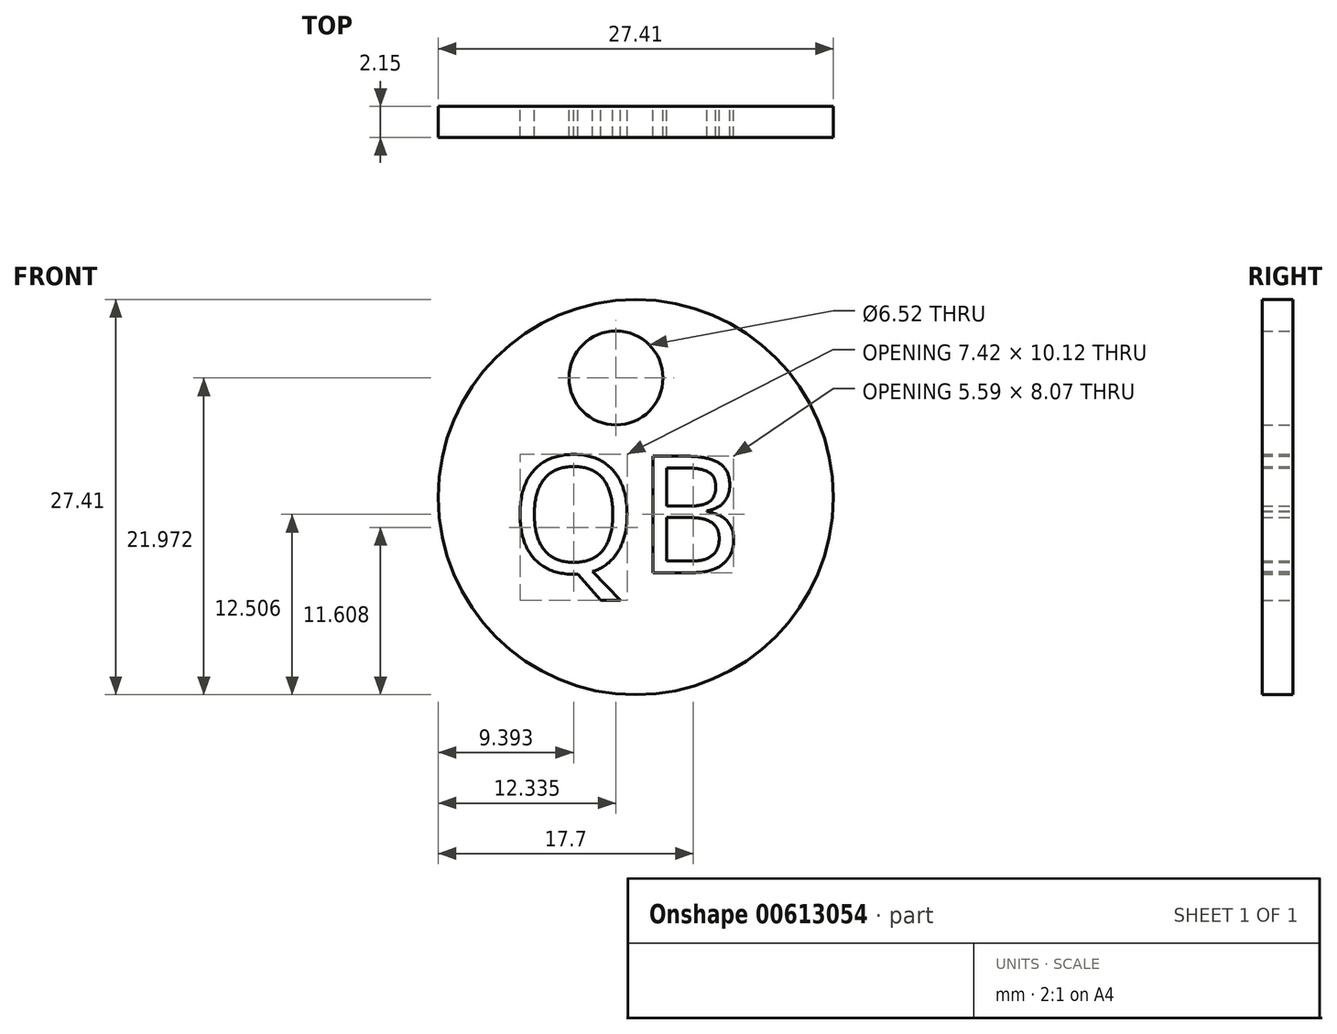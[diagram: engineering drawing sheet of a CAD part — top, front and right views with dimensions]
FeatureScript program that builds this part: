
annotation { "Feature Type Name" : "Feature", "Feature Type Description" : "" }
export const myFeature = defineFeature(function(context is Context, id is Id, definition is map)
    precondition{}
    {
        {
            var Q0;
            Q0=qCreatedBy(makeId("Front.planeOp"),FACE);
            var sketch = newSketch(context, id + "F0", { "sketchPlane" : qUnion([Q0])});
            skCircle(sketch, "E0", {"center": v(-43.44, -15.26) * mm, "radius": 13.7 * mm});
            skPoint(sketch, "E1", {"position": v(-42.95, -1.56) * mm});
            skPoint(sketch, "E2", {"position": v(-43.28, -28.96) * mm});
            skSolve(sketch);
        }
        {
            var Q0;
            Q0 = qSketchRegion(id + "F0", true);
            extrude(context, id + "F1", {"entities" : qUnion([Q0]), "depth" : 2.15 * mm, "offsetDistance" : 25 * mm});
        }
        {
            var Q0;
            Q0=qCreatedBy(makeId("Front.planeOp"),FACE);
            var sketch = newSketch(context, id + "F2", { "sketchPlane" : qUnion([Q0])});
            skCircle(sketch, "E3", {"center": v(-44.82, -6.99) * mm, "radius": 3.26 * mm});
            skSolve(sketch);
        }
        {
            var Q0;
            Q0 = qSketchRegion(id + "F2", true);
            var Q1;
            Q1=sQuery(id+"F2.wireOp",EDGE,"E3");
            extrude(context, id + "F3", {"entities" : qUnion([Q0]), "operationType" : NewBodyOperationType.REMOVE, "surfaceEntities" : qUnion([Q1]), "endBound" : BoundingType.UP_TO_NEXT, "depth" : 25 * mm, "offsetDistance" : 25 * mm});
        }
        {
            var Q0;
            Q0=qCreatedBy(makeId("Front.planeOp"),FACE);
            var sketch = newSketch(context, id + "F4", { "sketchPlane" : qUnion([Q0])});
            skText(sketch, "E4", { "text": "QB", "fontName": "OpenSans-Regular.ttf"});
            const initialGuessF4  = {"E4": [-0.05216, -0.02049, 1, 0, 0.00814]};
            skSetInitialGuess(sketch, initialGuessF4);
            skSolve(sketch);
        }
        {
            var Q0;
            Q0 = qSketchRegion(id + "F4", true);
            extrude(context, id + "F5", {"entities" : qUnion([Q0]), "operationType" : NewBodyOperationType.REMOVE, "endBound" : BoundingType.UP_TO_NEXT, "depth" : 25 * mm, "offsetDistance" : 25 * mm});
        }
    });
